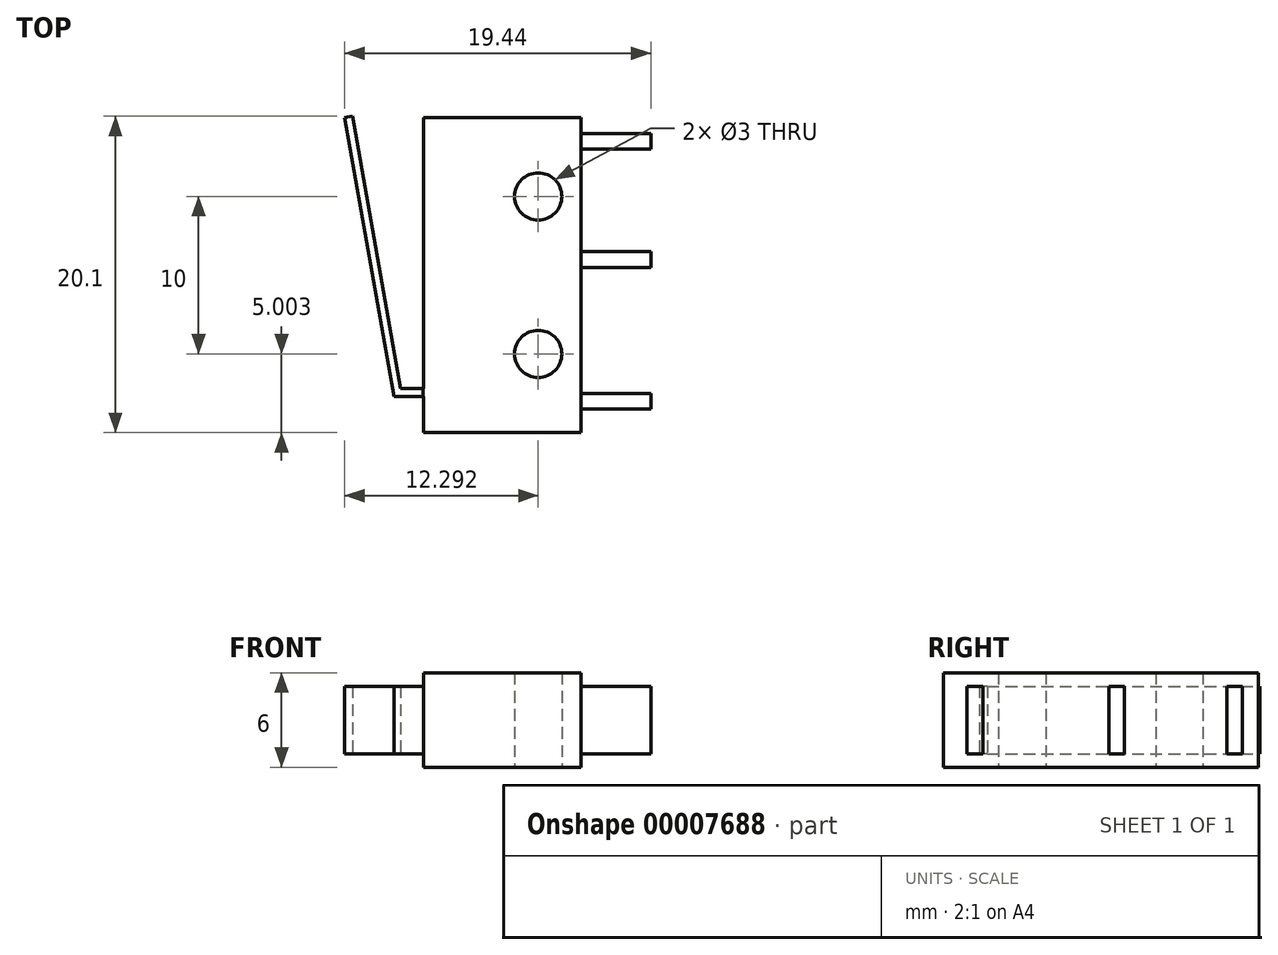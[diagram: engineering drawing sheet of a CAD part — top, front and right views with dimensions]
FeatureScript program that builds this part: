
annotation { "Feature Type Name" : "Feature", "Feature Type Description" : "" }
export const myFeature = defineFeature(function(context is Context, id is Id, definition is map)
    precondition{}
    {
        {
            var Q0;
            Q0=qCreatedBy(makeId("Top.planeOp"),FACE);
            var sketch = newSketch(context, id + "F0", { "sketchPlane" : qUnion([Q0])});
            skLineSegment(sketch, "E0.bottom", {"start": v(13.3, -13.06) * mm, "end": v(23.3, -13.06) * mm});
            skLineSegment(sketch, "E0.top", {"start": v(13.3, 6.94) * mm, "end": v(23.3, 6.94) * mm});
            skLineSegment(sketch, "E0.left", {"start": v(13.3, -13.06) * mm, "end": v(13.3, -10.76) * mm});
            skLineSegment(sketch, "E0.right", {"start": v(23.3, -13.06) * mm, "end": v(23.3, -11.56) * mm});
            skCircle(sketch, "E1", {"center": v(20.6, -8.06) * mm, "radius": 1.5 * mm});
            skCircle(sketch, "E2", {"center": v(20.6, 1.94) * mm, "radius": 1.5 * mm});
            skLineSegment(sketch, "E3.bottom", {"start": v(23.3, -11.56) * mm, "end": v(27.75, -11.56) * mm});
            skLineSegment(sketch, "E3.top", {"start": v(23.3, -10.56) * mm, "end": v(27.75, -10.56) * mm});
            skLineSegment(sketch, "E3.right", {"start": v(27.75, -11.56) * mm, "end": v(27.75, -10.56) * mm});
            skLineSegment(sketch, "E4.bottom", {"start": v(23.3, -1.56) * mm, "end": v(27.75, -1.56) * mm});
            skLineSegment(sketch, "E4.top", {"start": v(23.3, -2.56) * mm, "end": v(27.75, -2.56) * mm});
            skLineSegment(sketch, "E4.right", {"start": v(27.75, -1.56) * mm, "end": v(27.75, -2.56) * mm});
            skLineSegment(sketch, "E5.bottom", {"start": v(23.3, 5.94) * mm, "end": v(27.75, 5.94) * mm});
            skLineSegment(sketch, "E5.top", {"start": v(23.3, 4.94) * mm, "end": v(27.75, 4.94) * mm});
            skLineSegment(sketch, "E5.right", {"start": v(27.75, 5.94) * mm, "end": v(27.75, 4.94) * mm});
            skLineSegment(sketch, "E6.trimOffspring", {"start": v(23.3, -1.56) * mm, "end": v(23.3, 4.94) * mm});
            skLineSegment(sketch, "E7.trimOffspring", {"start": v(23.3, 5.94) * mm, "end": v(23.3, 6.94) * mm});
            skLineSegment(sketch, "E8.trimOffspring", {"start": v(23.3, -10.56) * mm, "end": v(23.3, -2.56) * mm});
            skLineSegment(sketch, "E9", {"start": v(13.3, -10.76) * mm, "end": v(11.43, -10.76) * mm});
            skLineSegment(sketch, "E10", {"start": v(11.43, -10.76) * mm, "end": v(8.31, 6.94) * mm});
            skLineSegment(sketch, "E11.0", {"start": v(11.85, -10.26) * mm, "end": v(8.8, 7.04) * mm});
            skLineSegment(sketch, "E11.1", {"start": v(13.3, -10.26) * mm, "end": v(11.85, -10.26) * mm});
            skLineSegment(sketch, "E12", {"start": v(8.31, 6.94) * mm, "end": v(8.8, 7.04) * mm});
            skLineSegment(sketch, "E13.trimOffspring", {"start": v(13.3, -10.26) * mm, "end": v(13.3, 6.94) * mm});
            skSolve(sketch);
        }
        {
            var Q0;
            Q0 = qSketchRegion(id + "F0", true);
            extrude(context, id + "F1", {"entities" : qUnion([Q0]), "depth" : 6 * mm});
        }
        {
            var Q0;
            Q0=makeQuery(id+"F1.opExtrude","SWEPT_FACE",FACE,{"disambiguationData":[OSD([sQuery(id+"F0.wireOp",EDGE,"E3.bottom")])]});
            var sketch = newSketch(context, id + "F2", { "sketchPlane" : qUnion([Q0])});
            skLineSegment(sketch, "E14.bottom", {"start": v(23.3, 6) * mm, "end": v(31.28, 6) * mm});
            skLineSegment(sketch, "E14.top", {"start": v(23.3, 5.15) * mm, "end": v(31.28, 5.15) * mm});
            skLineSegment(sketch, "E14.left", {"start": v(23.3, 6) * mm, "end": v(23.3, 5.15) * mm});
            skLineSegment(sketch, "E14.right", {"start": v(31.28, 6) * mm, "end": v(31.28, 5.15) * mm});
            skLineSegment(sketch, "E15.bottom", {"start": v(13.3, 6) * mm, "end": v(7.37, 6) * mm});
            skLineSegment(sketch, "E15.top", {"start": v(13.3, 5.15) * mm, "end": v(7.37, 5.15) * mm});
            skLineSegment(sketch, "E15.left", {"start": v(13.3, 6) * mm, "end": v(13.3, 5.15) * mm});
            skLineSegment(sketch, "E15.right", {"start": v(7.37, 6) * mm, "end": v(7.37, 5.15) * mm});
            skLineSegment(sketch, "E16.bottom", {"start": v(23.3, 0) * mm, "end": v(31.28, 0) * mm});
            skLineSegment(sketch, "E16.top", {"start": v(23.3, 0.85) * mm, "end": v(31.28, 0.85) * mm});
            skLineSegment(sketch, "E16.left", {"start": v(23.3, 0) * mm, "end": v(23.3, 0.85) * mm});
            skLineSegment(sketch, "E16.right", {"start": v(31.28, 0) * mm, "end": v(31.28, 0.85) * mm});
            skLineSegment(sketch, "E17.bottom", {"start": v(13.3, 0) * mm, "end": v(7.37, 0) * mm});
            skLineSegment(sketch, "E17.top", {"start": v(13.3, 0.85) * mm, "end": v(7.37, 0.85) * mm});
            skLineSegment(sketch, "E17.left", {"start": v(13.3, 0) * mm, "end": v(13.3, 0.85) * mm});
            skLineSegment(sketch, "E17.right", {"start": v(7.37, 0) * mm, "end": v(7.37, 0.85) * mm});
            skSolve(sketch);
        }
        {
            var Q0;
            Q0=makeQuery(id+"F2.imprint","IMPRINT",FACE,{"disambiguationData":[TD([[makeQuery(id+"F2.imprint","IMPRINT",EDGE,{"derivedFrom":sQuery(id+"F2.wireOp",EDGE,"E15.bottom")}),1.0]])]});
            var Q1;
            Q1=makeQuery(id+"F2.imprint","IMPRINT",FACE,{"disambiguationData":[TD([[makeQuery(id+"F2.imprint","IMPRINT",EDGE,{"derivedFrom":sQuery(id+"F2.wireOp",EDGE,"E17.bottom")}),-1.0]])]});
            var Q2;
            {var subQ5=sQuery(id+"F2.wireOp",EDGE,"E14.right");Q2=makeQuery(id+"F2.imprint","IMPRINT",FACE,{"disambiguationData":[TD([[makeQuery(id+"F2.imprint","IMPRINT",EDGE,{"derivedFrom":subQ5}),-1.0]])]});}
            var Q3;
            {var subQ5=sQuery(id+"F2.wireOp",EDGE,"E16.right");Q3=makeQuery(id+"F2.imprint","IMPRINT",FACE,{"disambiguationData":[TD([[makeQuery(id+"F2.imprint","IMPRINT",EDGE,{"derivedFrom":subQ5}),1.0]])]});}
            var Q4;
            {var subQ6=sQuery(id+"F2.wireOp",EDGE,"E16.left");Q4=makeQuery(id+"F2.imprint","IMPRINT",FACE,{"disambiguationData":[TD([[makeQuery(id+"F2.imprint","IMPRINT",EDGE,{"derivedFrom":subQ6}),1.0]])]});}
            var Q5;
            {var subQ6=sQuery(id+"F2.wireOp",EDGE,"E14.left");Q5=makeQuery(id+"F2.imprint","IMPRINT",FACE,{"disambiguationData":[TD([[makeQuery(id+"F2.imprint","IMPRINT",EDGE,{"derivedFrom":subQ6}),1.0]])]});}
            extrude(context, id + "F3", {"entities" : qUnion([Q0, Q1, Q2, Q3, Q4, Q5]), "operationType" : NewBodyOperationType.REMOVE, "endBound" : BoundingType.THROUGH_ALL, "oppositeDirection" : true, "depth" : 25 * mm});
        }
    });
